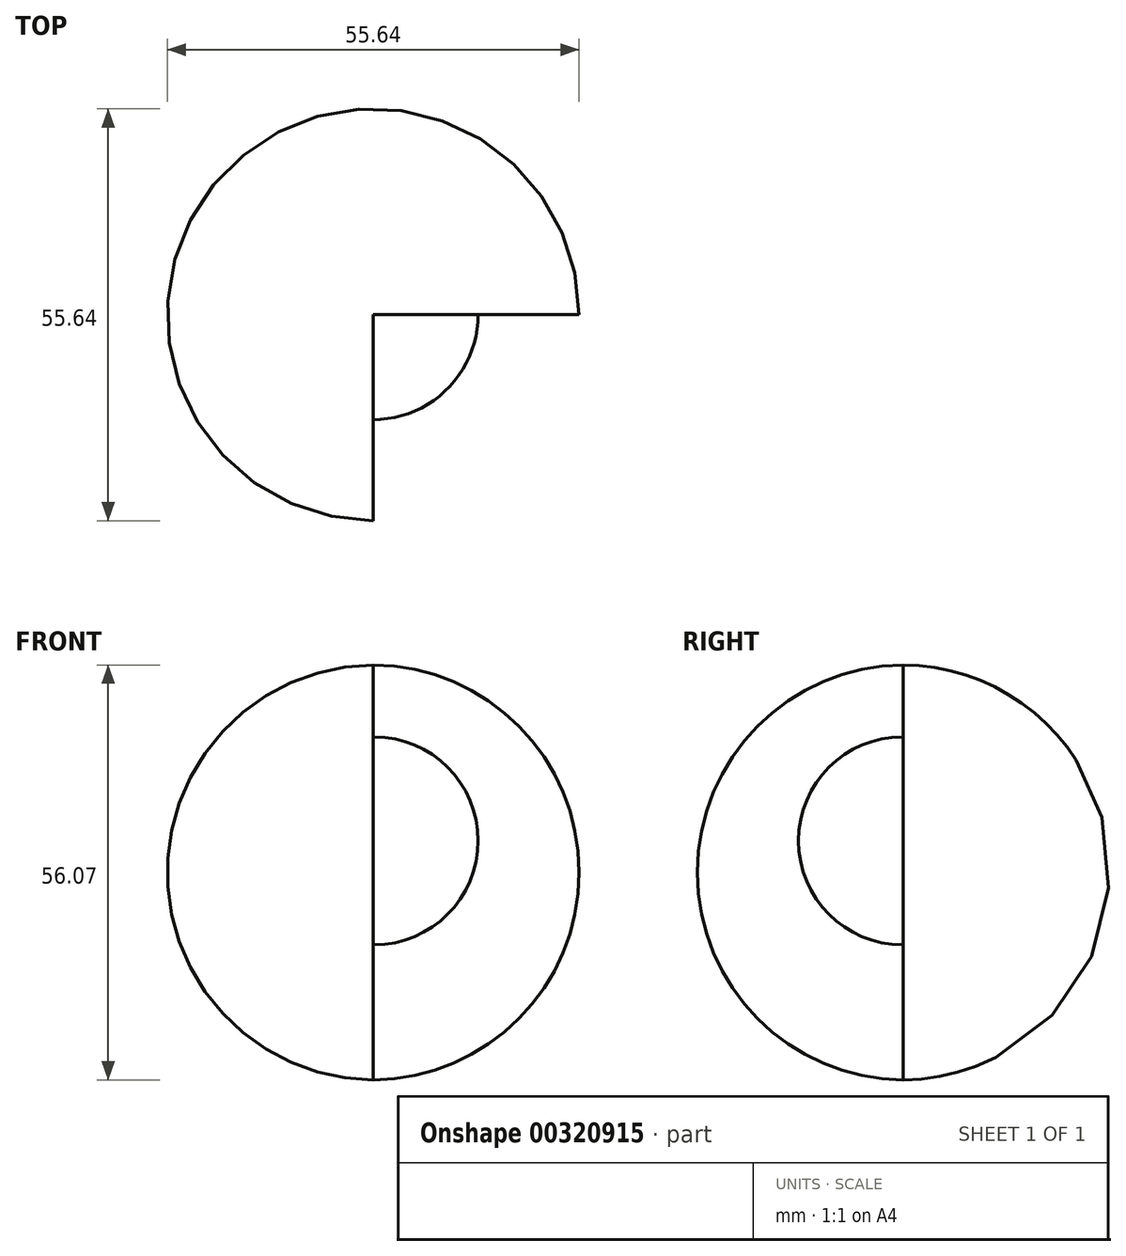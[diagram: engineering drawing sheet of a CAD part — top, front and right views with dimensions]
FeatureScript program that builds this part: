
annotation { "Feature Type Name" : "Feature", "Feature Type Description" : "" }
export const myFeature = defineFeature(function(context is Context, id is Id, definition is map)
    precondition{}
    {
        {
            var Q0;
            Q0=qCreatedBy(makeId("Front.planeOp"),FACE);
            var sketch = newSketch(context, id + "F0", { "sketchPlane" : qUnion([Q0])});
            skLineSegment(sketch, "E0", {"start": v(0, 0) * mm, "end": v(0, 56.07) * mm});
            skArc(sketch, "E1", {"start": v(0, 0) * mm, "mid": v(27.82, 28.03) * mm, "end": v(0, 56.07) * mm});
            skSolve(sketch);
        }
        {
            var Q0;
            Q0 = qSketchRegion(id + "F0", true);
            var Q1;
            Q1=sQuery(id+"F0.wireOp",EDGE,"E0");
            revolve(context, id + "F1", {"entities" : qUnion([Q0]), "axis" : qUnion([Q1]), "revolveType" : RevolveType.ONE_DIRECTION, "angle" : 270 * degree});
        }
        {
            var Q0;
            Q0=makeQuery(id+"F1.opRevolve","CAP_FACE",FACE,{"disambiguationData":[OSD([sQuery(id+"F0.wireOp",EDGE,"E0"),sQuery(id+"F0.wireOp",EDGE,"E1")])],"isStart":true});
            var sketch = newSketch(context, id + "F2", { "sketchPlane" : qUnion([Q0])});
            skLineSegment(sketch, "E2", {"start": v(0, 46.35) * mm, "end": v(0, 18.26) * mm});
            skArc(sketch, "E3", {"start": v(0, 18.26) * mm, "mid": v(14.17, 32.3) * mm, "end": v(0, 46.35) * mm});
            skSolve(sketch);
        }
        {
            var Q0;
            Q0 = qSketchRegion(id + "F2", true);
            var Q1;
            Q1=sQuery(id+"F2.wireOp",EDGE,"E2");
            revolve(context, id + "F3", {"operationType" : NewBodyOperationType.ADD, "entities" : qUnion([Q0]), "axis" : qUnion([Q1]), "revolveType" : RevolveType.FULL});
        }
    });
